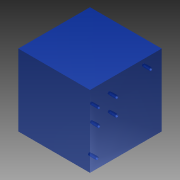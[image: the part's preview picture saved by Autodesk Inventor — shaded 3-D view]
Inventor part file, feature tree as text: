
AUTODESK INVENTOR PART (.ipt)
format: ipt  version: 2014 (Build 180170000, 170)  size: 183,808 bytes
history: native  units: mm
features: other x48, extrude x11, sketch x11
ambient origin geometry x8: Origin, YZ Plane, XZ Plane, XY Plane, X Axis, Y Axis, Z Axis, Center Point
bodies: 实体1 (feature_tree)
feature tree (70):
  extrude  "拉伸1"  Depth=14.0mm
  other  "UCS1"
  other  "UCS2"
  other  "UCS3"
  other  "UCS4"
  other  "UCS5"
  other  "UCS6"
  extrude  "拉伸2"  Depth=50.0mm
  extrude  "拉伸3"  Depth=44.0mm
  extrude  "拉伸4"  Depth=16.0mm
  extrude  "拉伸5"  Depth=32.0mm
  extrude  "拉伸6"  Depth=32.0mm
  extrude  "拉伸7"  Depth=32.0mm
  extrude  "拉伸8"  Depth=32.0mm
  extrude  "拉伸9"  Depth=32.0mm
  extrude  "拉伸10"  Depth=32.0mm TaperAngle=0.0deg
  extrude  "拉伸11"  Depth=32.0mm
  sketch  "草图1"  dims[d0=400.0mm d1=0.0mm]
  sketch  "草图2"  dims[d2=0.0mm d3=0.0mm d4=0.0mm d5=0.0mm d6=0.0mm d7=0.0mm]
  sketch  "草图3"  dims[d8=0.0mm d9=0.0mm d10=0.0mm d11=0.0mm d12=0.0mm d13=0.0mm]
  sketch  "草图4"  dims[d14=0.0mm d15=0.0mm d16=0.0mm d17=0.0mm d18=0.0mm d19=0.0mm]
  sketch  "草图5"  dims[d20=0.0mm d21=0.0mm d22=0.0mm d23=0.0mm d24=0.0mm d25=0.0mm]
  sketch  "草图6"  dims[d26=0.0mm d27=0.0mm d28=0.0mm d29=0.0mm d30=0.0mm d31=0.0mm]
  sketch  "草图7"  dims[d32=0.0mm d33=0.0mm d34=0.0mm d35=0.0mm d36=0.0mm d37=0.0mm d38=14.0mm]
  sketch  "草图8"  dims[d39=40.0mm d40=50.0mm]
  sketch  "草图9"  dims[d43=44.0mm d44=0.0mm d45=44.0mm d46=-10.297443mm]
  sketch  "草图10"  dims[d47=44.0mm d48=-10.297443mm d49=16.0mm]
  sketch  "草图11"  dims[d50=32.0mm d51=0.0mm d52=14.0mm d53=200.0mm d54=50.0mm d55=100.0mm d56=90.0mm d57=44.0mm d58=0.0mm d59=44.0mm d60=-10.297443mm d61=44.0mm d62=-10.297443mm d63=44.0mm d64=-10.297443mm d65=44.0mm d66=-10.297443mm d67=16.0mm d68=32.0mm d69=0.0mm d95=60.0mm d96=70.0mm]
  other  "UCS1: YZ 平面"
  other  "UCS1: XZ 平面"
  other  "UCS1: XY 平面"
  other  "UCS1: X 轴"
  other  "UCS1: Y 轴"
  other  "UCS1: Z 轴"
  other  "UCS1: 原点"
  other  "UCS2: YZ 平面"
  other  "UCS2: XZ 平面"
  other  "UCS2: XY 平面"
  other  "UCS2: X 轴"
  other  "UCS2: Y 轴"
  other  "UCS2: Z 轴"
  other  "UCS2: 原点"
  other  "UCS3: YZ 平面"
  other  "UCS3: XZ 平面"
  other  "UCS3: XY 平面"
  other  "UCS3: X 轴"
  other  "UCS3: Y 轴"
  other  "UCS3: Z 轴"
  other  "UCS3: 原点"
  other  "UCS4: YZ 平面"
  other  "UCS4: XZ 平面"
  other  "UCS4: XY 平面"
  other  "UCS4: X 轴"
  other  "UCS4: Y 轴"
  other  "UCS4: Z 轴"
  other  "UCS4: 原点"
  other  "UCS5: YZ 平面"
  other  "UCS5: XZ 平面"
  other  "UCS5: XY 平面"
  other  "UCS5: X 轴"
  other  "UCS5: Y 轴"
  other  "UCS5: Z 轴"
  other  "UCS5: 原点"
  other  "UCS6: YZ 平面"
  other  "UCS6: XZ 平面"
  other  "UCS6: XY 平面"
  other  "UCS6: X 轴"
  other  "UCS6: Y 轴"
  other  "UCS6: Z 轴"
  other  "UCS6: 原点"
